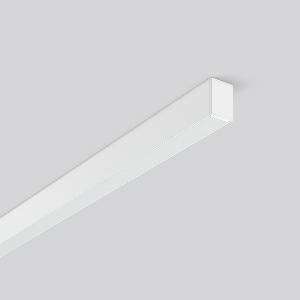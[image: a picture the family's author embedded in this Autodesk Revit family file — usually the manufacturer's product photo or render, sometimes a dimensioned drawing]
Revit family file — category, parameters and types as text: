
# Revit family: less_is_more_27_312201_002_1_a597
name_source: partatom
category: Lighting Fixtures
units: mm (PartAtom-declared; Revit-internal decimal feet)

## family parameters
Cut with Voids When Loaded = No
Host = Face
Light Source = No
Part Type = Normal
Room Calculation Point = No
Round Connector Dimension = Use Diameter
Shared = No

## types (1)
- LESS IS MORE 27 (1 x LED Modul 840, 3250 lm, 4000)
    Apparent Load = 39 VA
    CIE Flux Codes = 65 89 98 100 100
    Color Rendering = 80
    Color Temperature = 4000
    Default Elevation = 1800 mm
    Description = Series: LESS IS MORE 27
Ceiling luminaire with slim design. Housing: extruded aluminium profile, powder-coated. End cap aluminium powder-coated. Diffuser made of non-yellowing plastic (PMMA) microprismatic. Suitable for Ceiling mounting, Wall (surface). External driver with connecting cable. 
Colour: traffic white, matt (RAL 9016)
Length: 1512 mm
Width: 28 mm
Height: 38 mm
Lamp: LED
Socket: without socket
Colour temperature: 4000K
Colour rendering index (CRI): 82
System power: 39 W
Rated luminous flux: 3250 lm
Luminous efficiency: 83 lm/W
Control gear: Regulated power supply
Protection class: II
Type of protection: IP 20
    Height = 38 mm
    Lamp = 1 x LED Modul 840
    Lamp Light Flux = 3250 lm
    Lamp count = 1
    Length = 1512 mm
    Lifetime = 50000 h
    Luminous efficacy = 83 lm/W
    Manufacturer = RZB
    ModVariant = No
    Model = 312201.002.1
    Mounting Place = Ceiling, Wall
    Mounting Type = Surface mounted
    Number of Poles = 1
    OnlyDefault = Yes
    Power Factor = 1
    Product Name = LESS IS MORE 27
    Product group = Surface mounted LED linear luminaires
    ProductGroupID = 307
    Protection Class = Protection class II
    Protection Degree = IP 20
    RLX_Detail_Level = 1
    RLX_Emergency_Light_Flux = 0 lm
    RLX_Emergency_Type = 0
    RLX_Emergency_Type_DB = No
    RlxData = <blob elided: 24013 chars, md5=a3a8bba5>
    Socket = socket
    Standby Power = 0 W
    System Light Flux = 3250 lm
    System Power = 39 W
    Type Comments = Product without accessories
    Type Image = 312196.002.jpg
    URL = http://relux.com
    VarID = ---
    Voltage = 230 V
    Voltage Range = 220-240 V
    Weight = 0.00 kg
    Width = 28 mm

## geometry (parser evidence)
native form markers: Blend x4, Sweep x11
no freeform markers — native parametric forms only
